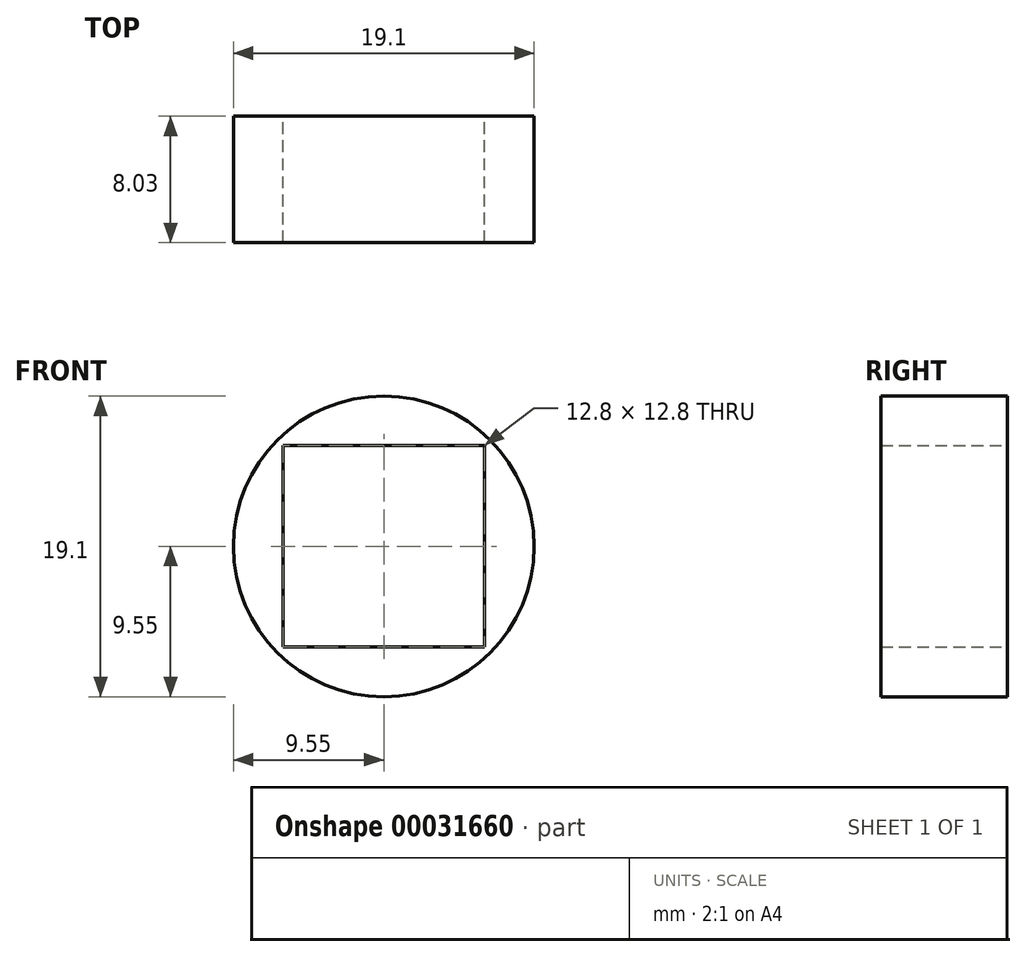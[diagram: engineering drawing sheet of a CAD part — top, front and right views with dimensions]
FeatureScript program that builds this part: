
annotation { "Feature Type Name" : "Feature", "Feature Type Description" : "" }
export const myFeature = defineFeature(function(context is Context, id is Id, definition is map)
    precondition{}
    {
        {
            var Q0;
            Q0=qCreatedBy(makeId("Front.planeOp"),FACE);
            var sketch = newSketch(context, id + "F0", { "sketchPlane" : qUnion([Q0])});
            skCircle(sketch, "E0", {"center": v(0, 0) * mm, "radius": 9.55 * mm});
            skLineSegment(sketch, "E1.rect.bottom", {"start": v(6.4, 6.4) * mm, "end": v(-6.4, 6.4) * mm});
            skLineSegment(sketch, "E1.rect.top", {"start": v(6.4, -6.4) * mm, "end": v(-6.4, -6.4) * mm});
            skLineSegment(sketch, "E1.rect.left", {"start": v(6.4, 6.4) * mm, "end": v(6.4, -6.4) * mm});
            skLineSegment(sketch, "E1.rect.right", {"start": v(-6.4, 6.4) * mm, "end": v(-6.4, -6.4) * mm});
            skSolve(sketch);
        }
        {
            var Q0;
            Q0=makeQuery(id+"F0.imprint","IMPRINT",FACE,{"disambiguationData":[TD([[makeQuery(id+"F0.imprint","IMPRINT",EDGE,{"derivedFrom":sQuery(id+"F0.wireOp",EDGE,"E0")}),1.0]])]});
            extrude(context, id + "F1", {"entities" : qUnion([Q0]), "depth" : 8.03 * mm});
        }
    });
